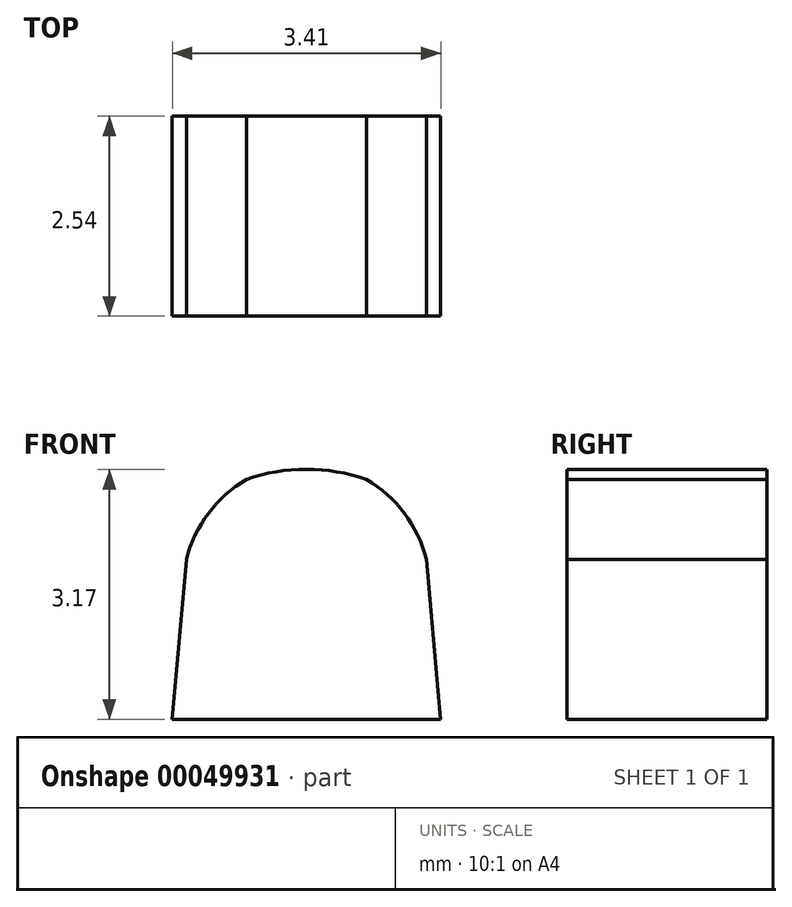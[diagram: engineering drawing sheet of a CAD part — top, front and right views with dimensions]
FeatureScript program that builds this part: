
annotation { "Feature Type Name" : "Feature", "Feature Type Description" : "" }
export const myFeature = defineFeature(function(context is Context, id is Id, definition is map)
    precondition{}
    {
        {
            var Q0;
            Q0=qCreatedBy(makeId("Front.planeOp"),FACE);
            var sketch = newSketch(context, id + "F0", { "sketchPlane" : qUnion([Q0])});
            skLineSegment(sketch, "E0", {"start": v(3.05, 2.03) * mm, "end": v(0, 2.03) * mm});
            skLineSegment(sketch, "E1", {"start": v(0, 2.03) * mm, "end": v(0, 3.05) * mm, "construction": true});
            skLineSegment(sketch, "E2", {"start": v(0, 3.05) * mm, "end": v(3.05, 3.05) * mm, "construction": true});
            skLineSegment(sketch, "E3", {"start": v(3.05, 2.03) * mm, "end": v(3.05, 3.05) * mm, "construction": true});
            skLineSegment(sketch, "E4", {"start": v(0, 3.05) * mm, "end": v(0.76, 3.05) * mm});
            skLineSegment(sketch, "E5", {"start": v(3.05, 3.05) * mm, "end": v(2.29, 3.05) * mm});
            skLineSegment(sketch, "E6", {"start": v(2.29, 3.05) * mm, "end": v(3.05, 2.03) * mm});
            skLineSegment(sketch, "E7", {"start": v(0.76, 3.05) * mm, "end": v(0, 2.03) * mm});
            skLineSegment(sketch, "E8", {"start": v(0.76, 3.05) * mm, "end": v(2.29, 3.05) * mm});
            skLineSegment(sketch, "E9", {"start": v(2.67, 2.54) * mm, "end": v(2.77, 2.62) * mm});
            skLineSegment(sketch, "E10", {"start": v(0.38, 2.54) * mm, "end": v(0.28, 2.62) * mm});
            skArc(sketch, "E11", {"start": v(0.76, 3.05) * mm, "mid": v(0.28, 2.62) * mm, "end": v(0, 2.03) * mm});
            skArc(sketch, "E12", {"start": v(3.05, 2.03) * mm, "mid": v(2.77, 2.62) * mm, "end": v(2.29, 3.05) * mm});
            skLineSegment(sketch, "E13", {"start": v(1.52, 3.05) * mm, "end": v(1.52, 3.18) * mm});
            skArc(sketch, "E14", {"start": v(2.29, 3.05) * mm, "mid": v(1.52, 3.18) * mm, "end": v(0.76, 3.05) * mm});
            skLineSegment(sketch, "E15", {"start": v(1.52, 0) * mm, "end": v(-0.18, 0) * mm});
            skLineSegment(sketch, "E16", {"start": v(1.52, 0) * mm, "end": v(3.23, 0) * mm});
            skLineSegment(sketch, "E17", {"start": v(1.52, 0) * mm, "end": v(1.52, 3.56) * mm});
            skLineSegment(sketch, "E18", {"start": v(-0.18, 0) * mm, "end": v(0, 2.03) * mm});
            skLineSegment(sketch, "E19", {"start": v(3.05, 2.03) * mm, "end": v(3.23, 0) * mm});
            skSolve(sketch);
        }
        {
            var Q0;
            Q0 = qSketchRegion(id + "F0", true);
            extrude(context, id + "F1", {"entities" : qUnion([Q0]), "depth" : 2.54 * mm});
        }
    });
